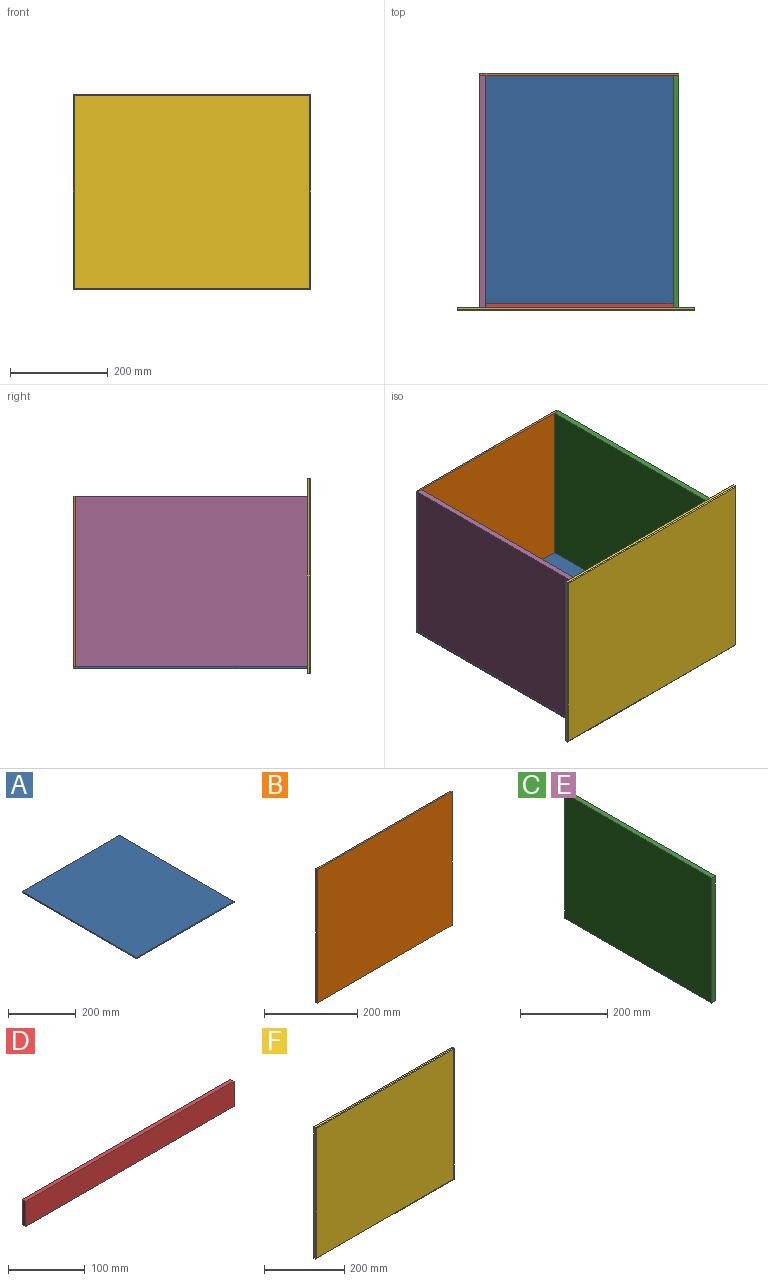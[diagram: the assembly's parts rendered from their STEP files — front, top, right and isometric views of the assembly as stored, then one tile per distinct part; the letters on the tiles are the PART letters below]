
ASSEMBLY  parts=6 mates=5
PART A: 6 faces, bbox 408x480x4 mm
  f0: plane 408x4mm, normal (0,-1,0), area 1632mm2, adj f1,f3,f4,f5
  f1: plane 480x4mm, normal (1,0,0), area 1920mm2, adj f0,f2,f4,f5
  f2: plane 408x4mm, normal (0,1,0), area 1632mm2, adj f1,f3,f4,f5
  f3: plane 480x4mm, normal (-1,0,0), area 1920mm2, adj f0,f2,f4,f5
  f4: plane 480x408mm, normal (0,0,1), area 195840mm2, adj f0,f1,f2,f3
  f5: plane 480x408mm, normal (0,0,-1), area 195840mm2, adj f0,f1,f2,f3
PART B: 6 faces, bbox 408x4x350 mm
  f0: plane 408x4mm, normal (0,0,-1), area 1632mm2, adj f1,f3,f4,f5
  f1: plane 350x4mm, normal (1,0,0), area 1400mm2, adj f0,f2,f4,f5
  f2: plane 408x4mm, normal (0,0,1), area 1632mm2, adj f1,f3,f4,f5
  f3: plane 350x4mm, normal (-1,0,0), area 1400mm2, adj f0,f2,f4,f5
  f4: plane 408x350mm, normal (0,-1,0), area 142800mm2, adj f0,f1,f2,f3
  f5: plane 408x350mm, normal (0,1,0), area 142800mm2, adj f0,f1,f2,f3
PART C: 6 faces, bbox 12x476x350 mm
  f0: plane 476x12mm, normal (0,0,-1), area 5712mm2, adj f1,f3,f4,f5
  f1: plane 350x12mm, normal (0,1,0), area 4200mm2, adj f0,f2,f4,f5
  f2: plane 476x12mm, normal (0,0,1), area 5712mm2, adj f1,f3,f4,f5
  f3: plane 350x12mm, normal (0,-1,0), area 4200mm2, adj f0,f2,f4,f5
  f4: plane 476x350mm, normal (1,0,0), area 166600mm2, adj f0,f1,f2,f3
  f5: plane 476x350mm, normal (-1,0,0), area 166600mm2, adj f0,f1,f2,f3
PART D: 6 faces, bbox 384x7x40 mm
  f0: plane 384x7mm, normal (0,0,-1), area 2688mm2, adj f1,f3,f4,f5
  f1: plane 40x7mm, normal (1,0,0), area 280mm2, adj f0,f2,f4,f5
  f2: plane 384x7mm, normal (0,0,1), area 2688mm2, adj f1,f3,f4,f5
  f3: plane 40x7mm, normal (-1,0,0), area 280mm2, adj f0,f2,f4,f5
  f4: plane 384x40mm, normal (0,-1,0), area 15360mm2, adj f0,f1,f2,f3
  f5: plane 384x40mm, normal (0,1,0), area 15360mm2, adj f0,f1,f2,f3
PART E: same geometry as C
PART F: 10 faces, bbox 488x7x400 mm
  f0: plane 488x5mm, normal (0,0,-1), area 2440mm2, adj f1,f3,f5,f6
  f1: plane 400x5mm, normal (1,0,0), area 2000mm2, adj f0,f2,f5,f7
  f2: plane 488x5mm, normal (0,0,1), area 2440mm2, adj f1,f3,f5,f9
  f3: plane 400x5mm, normal (-1,0,0), area 2000mm2, adj f0,f2,f5,f8
  f4: plane 484x396mm, normal (0,-1,0), area 191664mm2, adj f6,f7,f8,f9
  f5: plane 488x400mm, normal (0,1,0), area 195200mm2, adj f0,f1,f2,f3
  f6: cylinder r=2mm len=488mm, axis (-1,0,0), area 1528.5mm2, adj f0,f4,f7,f8
  f7: cylinder r=2mm len=400mm, axis (0,0,-1), area 1252.1mm2, adj f1,f4,f6,f9
  f8: cylinder r=2mm len=400mm, axis (0,0,1), area 1252.1mm2, adj f3,f4,f6,f9
  f9: cylinder r=2mm len=488mm, axis (1,0,0), area 1528.5mm2, adj f2,f4,f7,f8
PLACE A at identity
PLACE B t=(0,240,179)mm
PLACE C t=(192,-2,179)mm
PLACE D t=(0,-233,259)mm
PLACE E t=(-204,-2,179)mm
PLACE F t=(-7,-240,190)mm
MATE fastened A.f4 <-> B.f0  axis (0,0,1) through (-204,240,4)mm
MATE fastened A.f4 <-> E.f0  axis (0,0,1) through (-204,-240,4)mm
MATE fastened C.f0 <-> A.f4  axis (0,0,-1) through (204,-240,4)mm
MATE fastened F.f5 <-> A.f0  axis (0,1,0) through (-7,-240,-10)mm
MATE fastened D.f3 <-> E.f4  axis (-1,0,0) through (-192,-240,259)mm
